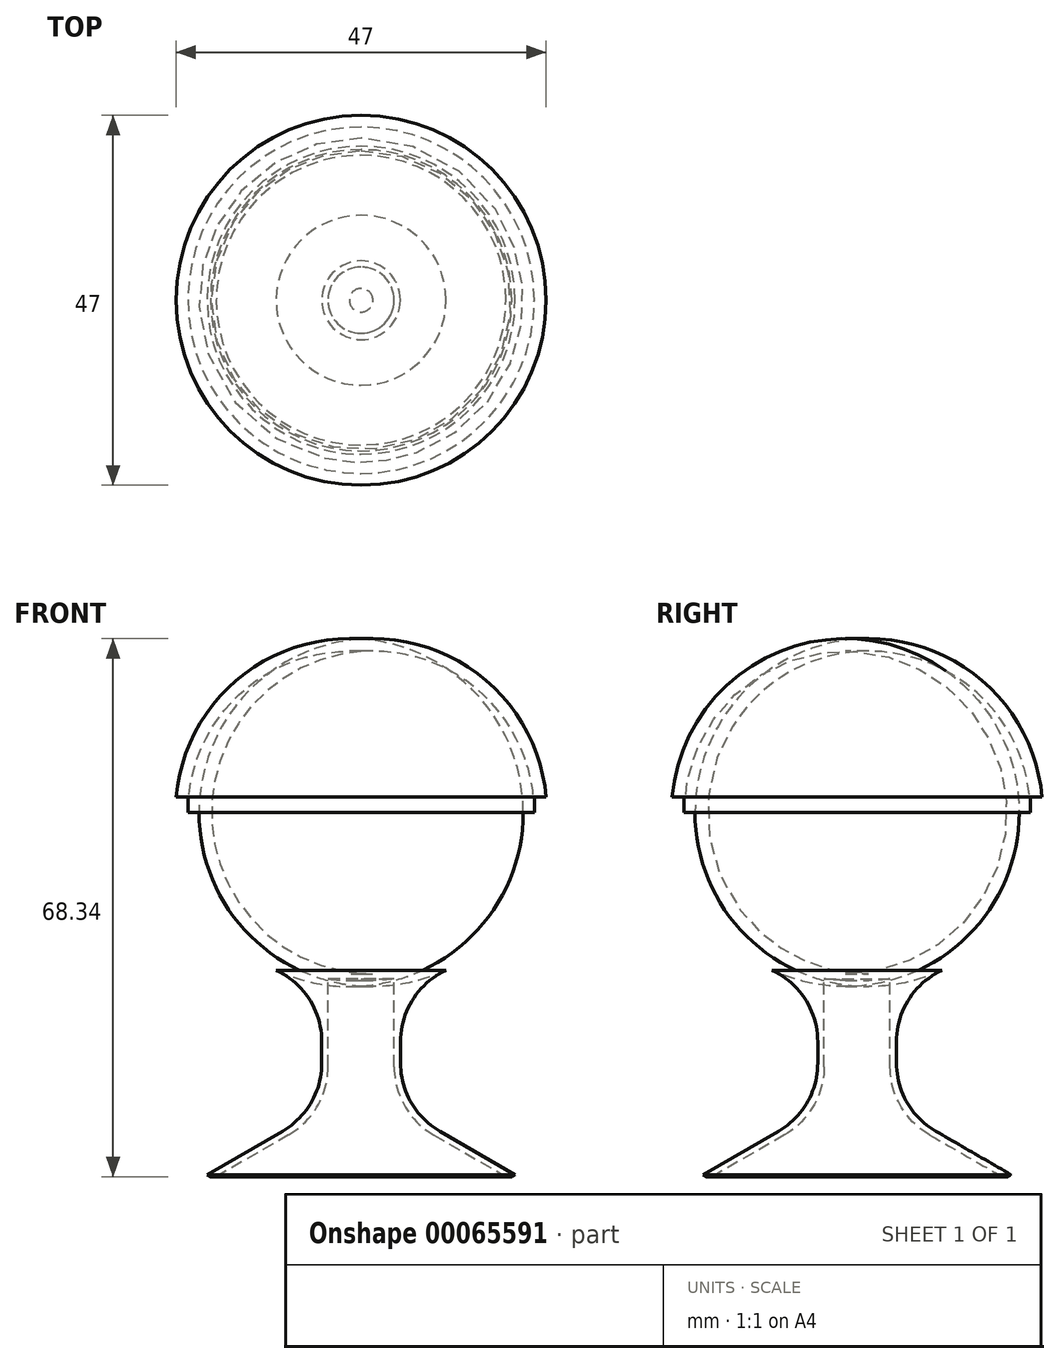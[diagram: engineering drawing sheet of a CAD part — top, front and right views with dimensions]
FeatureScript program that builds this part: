
annotation { "Feature Type Name" : "Feature", "Feature Type Description" : "" }
export const myFeature = defineFeature(function(context is Context, id is Id, definition is map)
    precondition{}
    {
        {
            var Q0;
            Q0=qCreatedBy(makeId("Right.planeOp"),FACE);
            var sketch = newSketch(context, id + "F0", { "sketchPlane" : qUnion([Q0])});
            skLineSegment(sketch, "E0", {"start": v(28.32, -13.8) * mm, "end": v(13.32, -5.13) * mm});
            skLineSegment(sketch, "E1", {"start": v(13.32, -5.13) * mm, "end": v(13.32, 10.65) * mm});
            skArc(sketch, "E2", {"start": v(13.32, 10.65) * mm, "mid": v(27.27, 18.91) * mm, "end": v(31.82, 34.46) * mm});
            skLineSegment(sketch, "E3", {"start": v(31.82, 34.46) * mm, "end": v(30.32, 34.46) * mm});
            skLineSegment(sketch, "E4", {"start": v(28.32, -13.8) * mm, "end": v(8.32, -13.8) * mm});
            skLineSegment(sketch, "E5", {"start": v(8.32, 11.96) * mm, "end": v(8.32, -13.8) * mm});
            skArc(sketch, "E6", {"start": v(9.82, 11.96) * mm, "mid": v(24.32, 17.97) * mm, "end": v(30.32, 32.46) * mm});
            skLineSegment(sketch, "E7", {"start": v(30.32, 34.46) * mm, "end": v(30.32, 32.46) * mm});
            skLineSegment(sketch, "E8", {"start": v(9.82, 11.96) * mm, "end": v(8.32, 11.96) * mm});
            skSolve(sketch);
        }
        {
            var Q0;
            Q0=makeQuery(id+"F0.imprint","IMPRINT",FACE,{"disambiguationData":[TD([[makeQuery(id+"F0.imprint","IMPRINT",EDGE,{"derivedFrom":sQuery(id+"F0.wireOp",EDGE,"E0")}),1.0]])]});
            var Q1;
            Q1=sQuery(id+"F0.wireOp",EDGE,"E5");
            revolve(context, id + "F1", {"entities" : qUnion([Q0]), "axis" : qUnion([Q1]), "revolveType" : RevolveType.FULL});
        }
        {
            var Q0;
            Q0=qCreatedBy(makeId("Right.planeOp"),FACE);
            var sketch = newSketch(context, id + "F2", { "sketchPlane" : qUnion([Q0])});
            skCircle(sketch, "E9", {"center": v(8.27, 22.71) * mm, "radius": 7.07 * mm});
            skLineSegment(sketch, "E10", {"start": v(8.27, 22.71) * mm, "end": v(8.27, -3.28) * mm, "construction": true});
            skSolve(sketch);
        }
        {
            var Q0;
            Q0 = qSketchRegion(id + "F2", true);
            extrude(context, id + "F3", {"entities" : qUnion([Q0]), "operationType" : NewBodyOperationType.REMOVE, "oppositeDirection" : true, "depth" : 40 * mm});
        }
        {
            var Q0;
            Q0=makeQuery(id+"F1.opRevolve","SWEPT_FACE",FACE,{"disambiguationData":[OSD([sQuery(id+"F0.wireOp",EDGE,"E4")])]});
            shell(context, id + "F4", {"entities" : qUnion([Q0]), "thickness" : 0.8 * mm});
        }
        {
            var Q0;
            Q0=makeQuery(id+"F1.opRevolve","SWEPT_EDGE",EDGE,{"disambiguationData":[OSD([sQuery(id+"F0.wireOp",EDGE,"E1"),sQuery(id+"F0.wireOp",EDGE,"E2")])]});
            var Q1;
            Q1=makeQuery(id+"F1.opRevolve","SWEPT_EDGE",EDGE,{"disambiguationData":[OSD([sQuery(id+"F0.wireOp",EDGE,"E0"),sQuery(id+"F0.wireOp",EDGE,"E1")])]});
            var Q2;
            Q2=makeQuery(id+"F4.opShell","OFFSET_EDGE",EDGE,{"disambiguationData":[OSD([sQuery(id+"F0.wireOp",EDGE,"E0"),sQuery(id+"F0.wireOp",EDGE,"E1")])]});
            fillet(context, id + "F5", {"entities" : qUnion([Q0, Q1, Q2]), "radius" : 10 * mm, "tangentPropagation" : true, "allowEdgeOverflow" : false});
        }
        {
            var Q0;
            Q0=makeQuery(id+"F1.opRevolve","SWEPT_EDGE",EDGE,{"disambiguationData":[OSD([sQuery(id+"F0.wireOp",EDGE,"E0"),sQuery(id+"F0.wireOp",EDGE,"E4")])]});
            chamfer(context, id + "F6", {"entities" : qUnion([Q0]), "chamferType" : ChamferType.OFFSET_ANGLE, "width" : .5 * mm, "oppositeDirection" : false, "angle" : 120 * degree, "tangentPropagation" : true});
        }
    });
